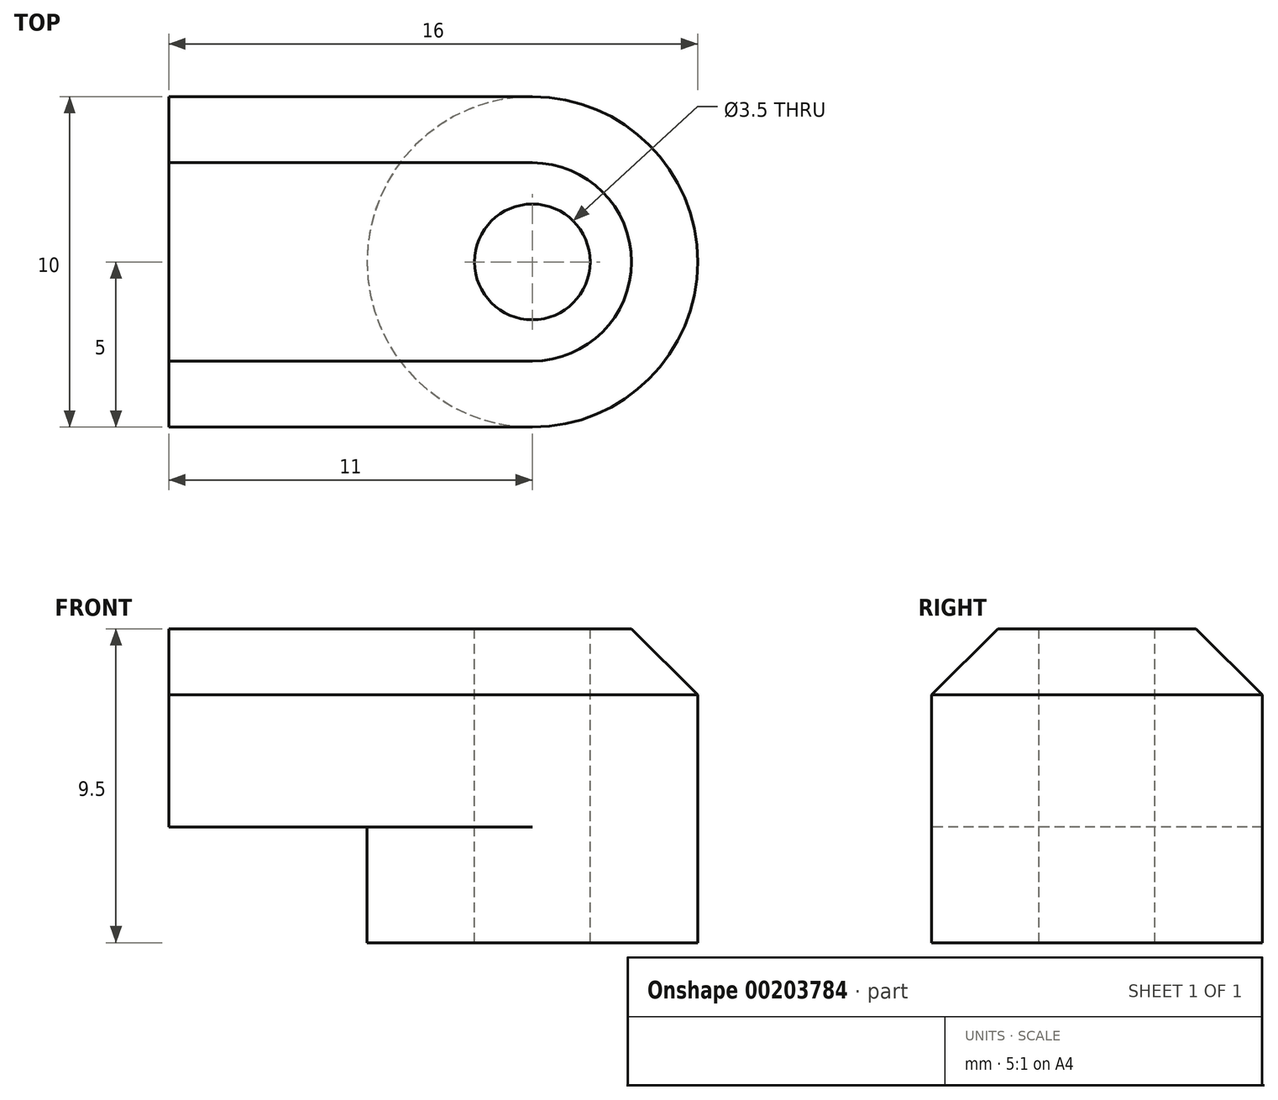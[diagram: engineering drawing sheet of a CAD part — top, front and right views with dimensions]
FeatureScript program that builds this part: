
annotation { "Feature Type Name" : "Feature", "Feature Type Description" : "" }
export const myFeature = defineFeature(function(context is Context, id is Id, definition is map)
    precondition{}
    {
        {
            var Q0;
            Q0=qCreatedBy(makeId("Top.planeOp"),FACE);
            var sketch = newSketch(context, id + "F0", { "sketchPlane" : qUnion([Q0])});
            skCircle(sketch, "E0", {"center": v(0, 0) * mm, "radius": 5 * mm});
            skCircle(sketch, "E1", {"center": v(0, 0) * mm, "radius": 1.75 * mm});
            skLineSegment(sketch, "E2", {"start": v(0, 5) * mm, "end": v(-11, 5) * mm});
            skLineSegment(sketch, "E3", {"start": v(-11, 5) * mm, "end": v(-11, -5) * mm});
            skLineSegment(sketch, "E4", {"start": v(-11, -5) * mm, "end": v(0, -5) * mm});
            skSolve(sketch);
        }
        {
            var Q0;
            {var subQ0=sQuery(id+"F0.wireOp",EDGE,"E2");Q0=makeQuery(id+"F0.imprint","IMPRINT",FACE,{"disambiguationData":[TD([[makeQuery(id+"F0.imprint","IMPRINT",EDGE,{"derivedFrom":subQ0}),1.0]])]});}
            extrude(context, id + "F1", {"entities" : qUnion([Q0]), "oppositeDirection" : true, "depth" : 6 * mm});
        }
        {
            var Q0;
            Q0=qCreatedBy(makeId("Top.planeOp"),FACE);
            var sketch = newSketch(context, id + "F2", { "sketchPlane" : qUnion([Q0])});
            skCircle(sketch, "E5", {"center": v(0, 0) * mm, "radius": 5 * mm});
            skCircle(sketch, "E6", {"center": v(0, 0) * mm, "radius": 1.75 * mm});
            skSolve(sketch);
        }
        {
            var Q0;
            Q0=makeQuery(id+"F2.imprint","IMPRINT",FACE,{"disambiguationData":[TD([[makeQuery(id+"F2.imprint","IMPRINT",EDGE,{"derivedFrom":sQuery(id+"F2.wireOp",EDGE,"E5")}),1.0]])]});
            extrude(context, id + "F3", {"entities" : qUnion([Q0]), "operationType" : NewBodyOperationType.ADD, "oppositeDirection" : true, "depth" : 9.5 * mm});
        }
        {
            var Q0;
            Q0=makeQuery(id+"F1.opExtrude","CAP_EDGE",EDGE,{"disambiguationData":[OSD([sQuery(id+"F0.wireOp",EDGE,"E2")])],"isStart":true});
            chamfer(context, id + "F4", {"entities" : qUnion([Q0]), "width" : 2 * mm, "tangentPropagation" : true});
        }
    });
